# Revit family: STE24
name_source: partatom
category: Lighting Fixtures
revit_build: Autodesk Revit Architecture 2012 (Build: 20110309_2315(x64)
units: mm (PartAtom-declared; Revit-internal decimal feet)

## types (9) — shared parameters
Backbox = White
Color Filter = 16777215
Default Elevation = 48.000"
Description = 2' × 4' Stratus® Recessed Indirect / 2-Lamp Twin Tube Cross Section
Dimming Lamp Color Temperature Shift = <None>
Emit from Line Length = 46.000"
Glass = Glass
Lamp = 3
Manufacturer = Columbia Lighting
Manufacturer Fax = 866.898.1065
Model = STE24
Product Documentation Link = http://www.columbialighting.com
Product Page URL = http://www.columbialighting.com
Tilt Angle = -90.00°
URL = http://www.columbialighting.com
Wattage Comments = 91W

## per-type parameters (varying)
| type | Photometric Web File |
| STE24-228G-MPO-EPU | itl67663.IES |
| STE24-232G-MPO-EU | ITL65806.IESÿ |
| STE24-254G-MPO-EPU | 3703.IES |
| STE24-328G-CLO-EPU | 3477.IES |
| STE24-328G-MPO-EPU | 3474.IES |
| STE24-332G-MPO-3EU-DG | 3464.IES |
| STE24-332G-MPO-EU | ITL65805.IES |
| STE24-328G-WPBMPO-EPU | 3475.IES |
| STE24-354G-MPO-EPU | 3708.IES |

## geometry (parser evidence)
native form markers: Sweep x1
no freeform markers — native parametric forms only
